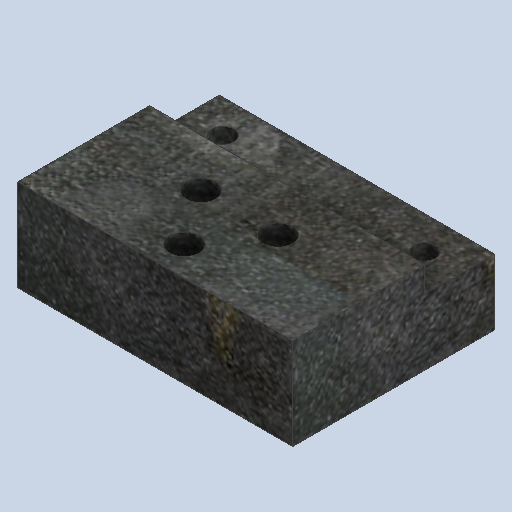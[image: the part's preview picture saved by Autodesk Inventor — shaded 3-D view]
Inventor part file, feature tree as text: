
AUTODESK INVENTOR PART (.ipt)
format: ipt  version: 2023.2 (Build 272271000, 271)  size: 395,776 bytes
history: native  units: mm
features: extrude x4, sketch x4
ambient origin geometry x8: Origin, YZ Plane, XZ Plane, XY Plane, X Axis, Y Axis, Z Axis, Center Point
bodies: Solid1 (feature_tree)
feature tree (8):
  extrude  "Extrusion1"  Depth=55.0mm
  extrude  "Extrusion2"  Depth=11.0mm
  extrude  "Extrusion3"  Depth=10.0mm
  extrude  "Extrusion4"  Depth=15.0mm
  sketch  "Sketch1"  dims[d0=75.0mm d1=55.0mm]
  sketch  "Sketch2"  dims[d2=11.0mm d4=11.0mm]
  sketch  "Sketch3"  dims[d6=55.0mm d7=10.0mm]
  sketch  "Sketch4"  dims[d8=10.0mm d9=15.0mm d11=15.0mm d13=15.0mm d15=23.0mm d16=8.0mm d17=21.0mm d18=10.5mm d19=46.0mm d20=7.0mm d21=0.0mm d22=6.0mm d23=6.0mm d24=15.0mm d25=15.0mm d26=15.0mm d27=8.0mm d28=8.0mm d29=8.0mm d30=55.0mm d31=10.0mm d32=10.0mm d33=46.0mm d34=23.0mm d35=8.0mm d36=10.5mm d37=10.5mm d38=21.0mm d39=3.0mm d40=0.0mm d41=6.0mm d42=8.0mm d43=8.0mm d44=8.0mm d45=8.0mm d46=23.0mm d47=10.5mm d48=10.5mm d49=8.0mm d50=0.0mm d51=75.0mm d52=36.0mm d53=8.0mm d54=8.0mm d55=8.0mm d56=8.0mm d57=23.0mm d58=21.0mm d59=10.5mm d60=7.0mm d61=0.0mm]
